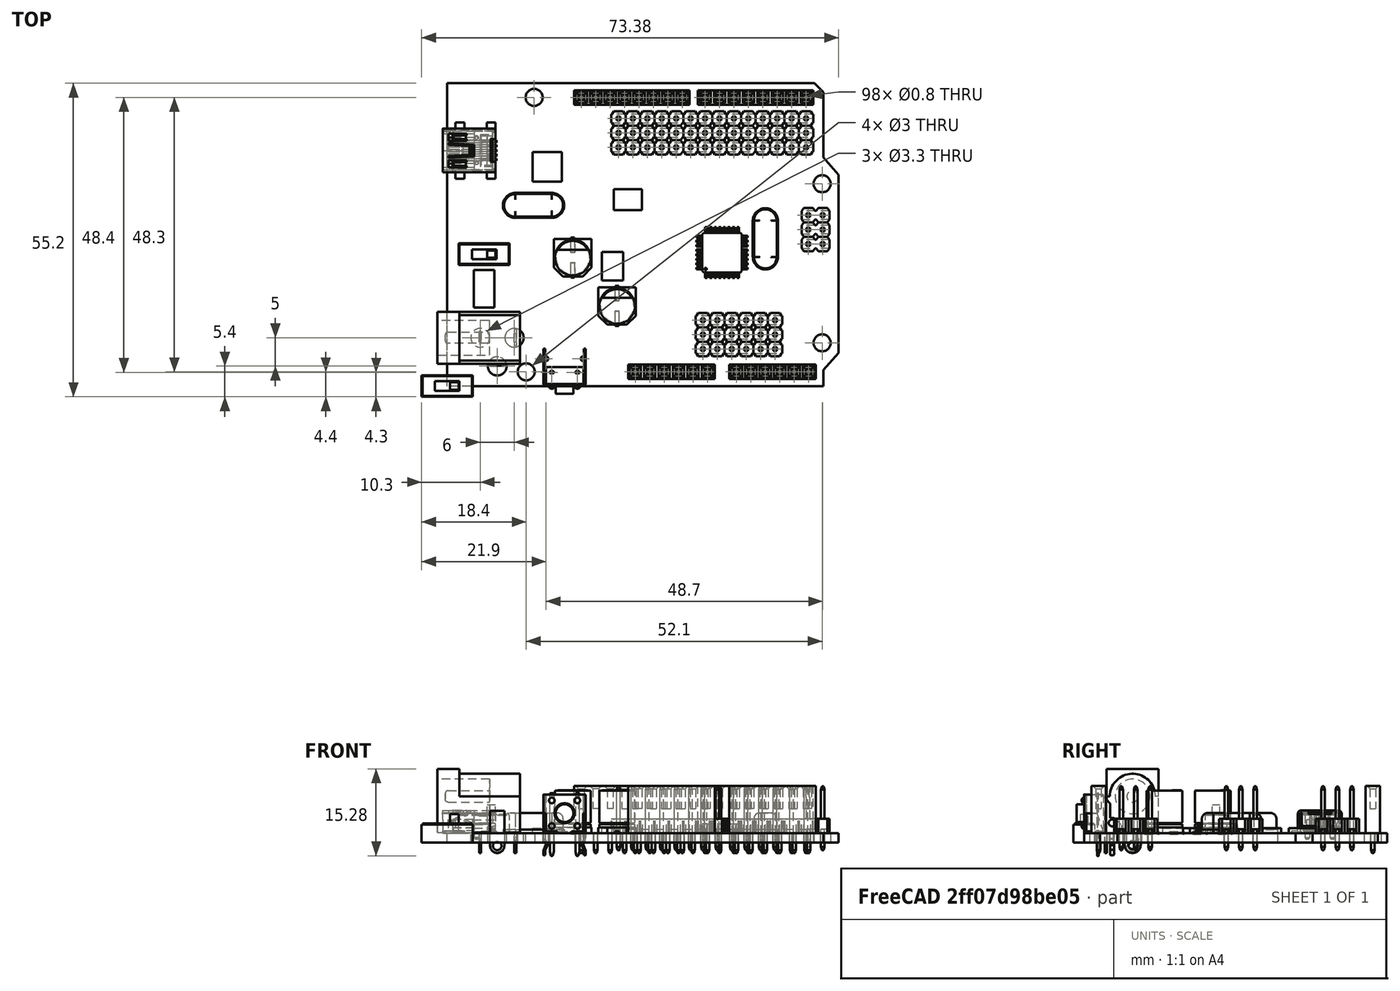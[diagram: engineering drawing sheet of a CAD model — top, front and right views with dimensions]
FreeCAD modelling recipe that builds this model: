
FCSTD DOCUMENT  (FreeCAD 0.14R3702 (Git))
Label: freaduino-uno
License: CC-BY 3.0
LicenseURL: http://creativecommons.org/licenses/by/3.0/
objects: Part::Compound×19, Part::FeaturePython×18, Part::Cylinder×12, Sketcher::SketchObject×9, PartDesign::Pad×7, Part::Feature×3, Part::MultiFuse×3, App::DocumentObjectGroup×3, PartDesign::Pocket×2, Part::Cut×1
note: 83 computed .brp shape members not serialized (recipe doc carries the construction recipe); baked Part::Feature solids carry a one-line shape summary decoded from their .brp

FEATURE [Sketcher::SketchObject] Sketch  label="pcb-main-body-sketch"
  sketch-geometry (9):
    g0: LineSegment StartX=66.2 StartY=0 StartZ=0 EndX=0 EndY=0 EndZ=0
    g1: LineSegment StartX=0 StartY=0 StartZ=0 EndX=0 EndY=53.3 EndZ=0
    g2: LineSegment StartX=66.2 StartY=51.7 StartZ=0 EndX=66.2 EndY=40.2 EndZ=0
    g3: LineSegment StartX=66.2 StartY=40.2 StartZ=0 EndX=68.88 EndY=37.2 EndZ=0
    g4: LineSegment StartX=68.88 StartY=37.2 StartZ=0 EndX=68.88 EndY=5.8 EndZ=0
    g5: LineSegment StartX=68.88 StartY=5.8 StartZ=0 EndX=66.2 EndY=2.8 EndZ=0
    g6: LineSegment StartX=66.2 StartY=2.8 StartZ=0 EndX=66.2 EndY=0 EndZ=0
    g7: LineSegment StartX=0 StartY=53.3 StartZ=0 EndX=64.6 EndY=53.3 EndZ=0
    g8: LineSegment StartX=64.6 StartY=53.3 StartZ=0 EndX=66.2 EndY=51.7 EndZ=0
  constraints (26):
    c: Coincident(g0,g1)
    c: Horizontal(g0)
    c: Vertical(g1)
    c: Coincident(g0,g-1)
    c: Coincident(g2,g3)
    c: Coincident(g3,g4)
    c: Coincident(g4,g5)
    c: Coincident(g5,g6)
    c: Coincident(g6,g0)
    c: DistanceY(g1) = 53.3
    c: Vertical(g6)
    c: Vertical(g2)
    c: Vertical(g4)
    c: PointOnObject(g0,g2)
    c: DistanceY(g2,g3) = -3
    c: DistanceY(g2,g5) = -37.4
    c: DistanceX(g2,g3) = 2.68
    c: Coincident(g7,g8)
    c: Horizontal(g7)
    c: Coincident(g7,g1)
    c: Coincident(g8,g2)
    c: DistanceX(g2,g1) = -66.2
    c: Angle(g7,g8) = 2.35619
    c: DistanceX(g7,g2) = 1.6
    c: DistanceY(g2) = -11.5
    c: DistanceY(g4,g5) = -3
FEATURE [PartDesign::Pad] Pad  label="pcb-main-body"
  Length = 1.7
  Length2 = 100
  Sketch = -> Sketch
  Type = 0
FEATURE [Sketcher::SketchObject] Sketch001  label="pcb-attachment-drills-sketch"
  ExternalGeometry = -> [Pad]
  Placement = pos=(0,0,1.7) rot=(0,0,1;0rad)
  Support = -> Pad [Face11]
  sketch-geometry (5):
    g0: Circle CenterX=15.3 CenterY=50.8 CenterZ=0 NormalX=0 NormalY=0 NormalZ=1 Radius=1.5
    g1: Circle CenterX=13.9 CenterY=2.5 CenterZ=0 NormalX=0 NormalY=0 NormalZ=1 Radius=1.5
    g2: Circle CenterX=66 CenterY=35.6 CenterZ=0 NormalX=0 NormalY=0 NormalZ=1 Radius=1.5
    g3: Circle CenterX=66 CenterY=7.6 CenterZ=0 NormalX=0 NormalY=0 NormalZ=1 Radius=1.5
    g4: LineSegment [constr] StartX=66 StartY=35.6 StartZ=0 EndX=66 EndY=7.6 EndZ=0
  constraints (14):
    c: Radius(g1) = 1.5
    c: Equal(g1,g0)
    c: Equal(g0,g2)
    c: Equal(g2,g3)
    c: DistanceX(g-1,g1) = 13.9
    c: DistanceY(g-1,g1) = 2.5
    c: DistanceY(g-1,g0) = 50.8
    c: Vertical(g4)
    c: Coincident(g4,g2)
    c: Coincident(g4,g3)
    c: DistanceX(g-1,g0) = 15.3
    c: DistanceY(g4) = -28
    c: DistanceY(g1,g3) = 5.1
    c: DistanceX(g1,g3) = 52.1
FEATURE [PartDesign::Pocket] Pocket  label="pcb-attachment-drills"
  Length = 5
  Sketch = -> Sketch001
  Type = 1
FEATURE [Part::Cylinder] Cylinder
  Angle = 360
  Height = 10
  Placement = pos=(0,0,-4) rot=(0,0,1;0rad)
  Radius = 0.4
FEATURE [Part::FeaturePython] Array  label="drills-1"  # Draft array (typed FeaturePython)
  Angle = 360
  ArrayType = 0
  Axis = (0,0,1)
  Base = -> Cylinder
  Center = (0,0,0)
  IntervalX = (2.54,0,0)
  IntervalY = (0,1,0)
  IntervalZ = (0,0,1)
  NumberPolar = 1
  NumberX = 6
  NumberY = 1
  NumberZ = 1
  Placement = pos=(33.1,2.5,0) rot=(0,0,1;0rad)
FEATURE [Part::Feature] Array001  label="drills-002"
  Placement = pos=(50.9,2.5,0) rot=(0,0,1;0rad)
  shape: bbox 13.5 x 0.8 x 10 mm, 18 faces, 6 solids (baked)
FEATURE [Part::Cylinder] Cylinder001
  Angle = 360
  Height = 10
  Placement = pos=(0,0,-3) rot=(0,0,1;0rad)
  Radius = 0.4
FEATURE [Part::FeaturePython] Array002  label="drills-003"  # Draft array (typed FeaturePython)
  Angle = 360
  ArrayType = 0
  Axis = (0,0,1)
  Base = -> Cylinder001
  Center = (0,0,0)
  IntervalX = (2.54,0,0)
  IntervalY = (0,1,0)
  IntervalZ = (0,0,1)
  NumberPolar = 1
  NumberX = 8
  NumberY = 1
  NumberZ = 1
  Placement = pos=(23.6,50.8,0) rot=(0,0,1;0rad)
FEATURE [Part::Feature] Array002001  label="drills-004"
  Placement = pos=(45.38,50.8,0) rot=(0,0,1;0rad)
  shape: bbox 18.58 x 0.8 x 10 mm, 24 faces, 8 solids (baked)
FEATURE [Part::Cylinder] Cylinder002  label="cylinder"
  Angle = 360
  Height = 10
  Placement = pos=(63.16,47.1,-3) rot=(0,0,1;0rad)
  Radius = 0.4
FEATURE [Part::FeaturePython] Array002002  # Draft array (typed FeaturePython)
  Angle = 360
  ArrayType = 0
  Axis = (0,0,1)
  Base = -> Cylinder002
  Center = (0,0,0)
  IntervalX = (-2.54,0,0)
  IntervalY = (0,1,0)
  IntervalZ = (0,0,1)
  NumberPolar = 1
  NumberX = 14
  NumberY = 0
  NumberZ = 1
FEATURE [Part::FeaturePython] Array002003  label="drills-digital"  # Draft array (typed FeaturePython)
  Angle = 360
  ArrayType = 0
  Axis = (0,0,1)
  Base = -> Array002002
  Center = (0,0,0)
  IntervalX = (1,0,0)
  IntervalY = (0,-2.54,0)
  IntervalZ = (0,0,1)
  NumberPolar = 1
  NumberX = 1
  NumberY = 3
  NumberZ = 1
FEATURE [Part::Cylinder] Cylinder003  label="Cylinder002"
  Angle = 360
  Height = 10
  Placement = pos=(45,6.5,-3) rot=(0,0,1;0rad)
  Radius = 0.4
FEATURE [Part::FeaturePython] Array002004  # Draft array (typed FeaturePython)
  Angle = 360
  ArrayType = 0
  Axis = (0,0,1)
  Base = -> Cylinder003
  Center = (0,0,0)
  IntervalX = (2.54,0,0)
  IntervalY = (0,1,0)
  IntervalZ = (0,0,1)
  NumberPolar = 1
  NumberX = 6
  NumberY = 1
  NumberZ = 1
FEATURE [Part::FeaturePython] Array002005  label="drills-analog"  # Draft array (typed FeaturePython)
  Angle = 360
  ArrayType = 0
  Axis = (0,0,1)
  Base = -> Array002004
  Center = (0,0,0)
  IntervalX = (1,0,0)
  IntervalY = (0,2.54,0)
  IntervalZ = (0,0,1)
  NumberPolar = 1
  NumberX = 1
  NumberY = 3
  NumberZ = 1
FEATURE [Part::Cylinder] Cylinder004  label="Cylinder003"
  Angle = 360
  Height = 10
  Placement = pos=(66.1,25,-3) rot=(0,0,1;0rad)
  Radius = 0.4
FEATURE [Part::FeaturePython] Array002006  # Draft array (typed FeaturePython)
  Angle = 360
  ArrayType = 0
  Axis = (0,0,1)
  Base = -> Cylinder004
  Center = (0,0,0)
  IntervalX = (-2.54,0,0)
  IntervalY = (0,0,0)
  IntervalZ = (0,0,1)
  NumberPolar = 1
  NumberX = 2
  NumberY = 1
  NumberZ = 1
FEATURE [Part::FeaturePython] Array002007  label="drills-icsp"  # Draft array (typed FeaturePython)
  Angle = 360
  ArrayType = 0
  Axis = (0,0,1)
  Base = -> Array002006
  Center = (0,0,0)
  IntervalX = (1,0,0)
  IntervalY = (0,2.54,0)
  IntervalZ = (0,0,1)
  NumberPolar = 1
  NumberX = 1
  NumberY = 3
  NumberZ = 1
FEATURE [Part::Cylinder] Cylinder005  label="Cylinder004"
  Angle = 360
  Height = 10
  Placement = pos=(18.4,2.4,-3) rot=(0,0,1;0rad)
  Radius = 0.4
FEATURE [Part::Cylinder] Cylinder006  label="Cylinder005"
  Angle = 360
  Height = 10
  Placement = pos=(22.91,2.4,-3) rot=(0,0,1;0rad)
  Radius = 0.4
FEATURE [Part::Cylinder] Cylinder007  label="Cylinder006"
  Angle = 360
  Height = 10
  Placement = pos=(17.4,4.8,-3) rot=(0,0,1;0rad)
  Radius = 0.4
FEATURE [Part::Cylinder] Cylinder008  label="Cylinder007"
  Angle = 360
  Height = 10
  Placement = pos=(23.91,4.8,-3) rot=(0,0,1;0rad)
  Radius = 0.4
FEATURE [Part::MultiFuse] Fusion  label="reset-button-drills"
  Shapes = -> [Cylinder005,Cylinder006,Cylinder007,Cylinder008]
FEATURE [Part::Cylinder] Cylinder009  label="Cylinder008"
  Angle = 360
  Height = 10
  Placement = pos=(0,0,-3) rot=(0,0,1;0rad)
  Radius = 1.65
FEATURE [Part::Cylinder] Cylinder010  label="Cylinder009"
  Angle = 360
  Height = 10
  Placement = pos=(3,5,-3) rot=(0,0,1;0rad)
  Radius = 1.65
FEATURE [Part::Cylinder] Cylinder011  label="Cylinder010"
  Angle = 360
  Height = 10
  Placement = pos=(-3,5,-3) rot=(0,0,1;0rad)
  Radius = 1.65
FEATURE [Part::MultiFuse] Fusion001  label="power-jack-drills"
  Placement = pos=(8.8,3.5,0) rot=(0,0,1;0rad)
  Shapes = -> [Cylinder009,Cylinder011,Cylinder010]
FEATURE [Part::MultiFuse] Fusion002  label="cylinders-drills"
  Shapes = -> [Array,Array002003,Array002,Array002001,Array001,Array002005,Array002007,Fusion001,Fusion]
FEATURE [Part::Cut] Cut  label="pcb-with-drills"
  Base = -> Pocket
  Tool = -> Fusion002
FEATURE [Part::Compound] Compound  label="1x6-female-pin-header"
  Placement = pos=(50.9,2.5,1.7) rot=(0,0,1;0rad)
FEATURE [Part::Compound] Compound001  label="1x6-female-pin-header001"
  Placement = pos=(33.1,2.5,1.7) rot=(0,0,1;0rad)
FEATURE [Part::Compound] Compound002  label="1x8-female-pin-header"
  Placement = pos=(45.4,50.8,1.7) rot=(0,0,1;0rad)
FEATURE [Part::Compound] Compound003  label="1x8-female-pin-header001"
  Placement = pos=(23.6,50.8,1.7) rot=(0,0,1;0rad)
FEATURE [Part::Compound] Compound004  label="1x14-male-pin-header"
  Placement = pos=(30.14,47.1,1.7) rot=(0,0,1;0rad)
FEATURE [Part::Compound] Compound005  label="1x14-male-pin-header001"
  Placement = pos=(30.14,42.02,1.7) rot=(0,0,1;0rad)
FEATURE [Part::Compound] Compound006  label="1x14-male-pin-header002"
  Placement = pos=(30.14,44.56,1.698) rot=(0,0,1;0rad)
FEATURE [Part::Compound] Compound007  label="1x6-male-pin-header"
  Links = -> [Array001,Array002001]
  Placement = pos=(45,6.5,1.7) rot=(0,0,1;0rad)
FEATURE [Part::Compound] Compound008  label="1x6-male-pin-header001"
  Links = -> [Array001,Array002001]
  Placement = pos=(45,9.04,1.7) rot=(0,0,1;0rad)
FEATURE [Part::Compound] Compound009  label="1x6-male-pin-header002"
  Links = -> [Array001,Array002001]
  Placement = pos=(45,11.58,1.7) rot=(0,0,1;0rad)
FEATURE [Part::Compound] Compound010  label="2x3-male-pin-header"
  Placement = pos=(64.83,27.54,1.7) rot=(0,0,1;0rad)
FEATURE [Part::Compound] Compound011  label="pushbutton-right-angle"
  Placement = pos=(20.6546,4.9,1.69239) rot=(0,0,1;0rad)
FEATURE [Part::Feature] Fusion003  label="jack_DC_2.1mm_PCB-final"
  Placement = pos=(-1.7,8.5,1.8) rot=(0.57735,-0.57735,-0.57735;2.0944rad)
  shape: bbox 14.48 x 9.472 x 14.78 mm, 34 faces (baked)
FEATURE [Part::Compound] Compound012  label="micro-usb-b-female-smd"
  Placement = pos=(8,41.45,1.7667) rot=(0.57735,-0.57735,-0.57735;2.0944rad)
FEATURE [Part::FeaturePython] Clone  label="Xtal"  # WARN: FeaturePython — macro-defined, semantics opaque (R4)
  Placement = pos=(15.2,31.8,1) rot=(0,0,1;0rad)
  Scale = (1,1,1)
FEATURE [Part::FeaturePython] Clone001  label="Xtal001"  # WARN: FeaturePython — macro-defined, semantics opaque (R4)
  Placement = pos=(56,25.9,1) rot=(0,0,1;1.5708rad)
  Scale = (1,1,1)
FEATURE [Part::Compound] Compound013  label="PQFP-32"
  Placement = pos=(43.86,19,1.7) rot=(0,0,1;0rad)
FEATURE [Sketcher::SketchObject] Sketch002  label="switch-body-sketch"
  sketch-geometry (4):
    g0: LineSegment StartX=-4.5 StartY=1.9 StartZ=0 EndX=4.5 EndY=1.9 EndZ=0
    g1: LineSegment StartX=4.5 StartY=1.9 StartZ=0 EndX=4.5 EndY=-1.9 EndZ=0
    g2: LineSegment StartX=4.5 StartY=-1.9 StartZ=0 EndX=-4.5 EndY=-1.9 EndZ=0
    g3: LineSegment StartX=-4.5 StartY=-1.9 StartZ=0 EndX=-4.5 EndY=1.9 EndZ=0
  constraints (11):
    c: Coincident(g0,g1)
    c: Coincident(g1,g2)
    c: Coincident(g2,g3)
    c: Coincident(g3,g0)
    c: Horizontal(g0)
    c: Horizontal(g2)
    c: Vertical(g1)
    c: Vertical(g3)
    c: DistanceX(g0) = 9
    c: DistanceY(g1) = -3.8
    c: Symmetric(g0,g1,g-1)
FEATURE [PartDesign::Pad] Pad001  label="switch-body"
  Length = 3.2
  Length2 = 100
  Sketch = -> Sketch002
  Type = 0
FEATURE [Sketcher::SketchObject] Sketch003  label="switch-top-plate-body-sketch"
  Placement = pos=(0,0,3.2) rot=(0,0,1;0rad)
  sketch-geometry (4):
    g0: LineSegment StartX=-4.35 StartY=1.725 StartZ=0 EndX=4.35 EndY=1.725 EndZ=0
    g1: LineSegment StartX=4.35 StartY=1.725 StartZ=0 EndX=4.35 EndY=-1.725 EndZ=0
    g2: LineSegment StartX=4.35 StartY=-1.725 StartZ=0 EndX=-4.35 EndY=-1.725 EndZ=0
    g3: LineSegment StartX=-4.35 StartY=-1.725 StartZ=0 EndX=-4.35 EndY=1.725 EndZ=0
  constraints (11):
    c: Coincident(g0,g1)
    c: Coincident(g1,g2)
    c: Coincident(g2,g3)
    c: Coincident(g3,g0)
    c: Horizontal(g0)
    c: Horizontal(g2)
    c: Vertical(g1)
    c: Vertical(g3)
    c: Symmetric(g0,g1,g-1)
    c: DistanceX(g0) = 8.7
    c: DistanceY(g1) = -3.45
FEATURE [PartDesign::Pad] Pad002  label="switch-top-plate-body"
  Length = 0.2
  Length2 = 100
  Placement = pos=(0,0,3.2) rot=(0,0,1;0rad)
  Sketch = -> Sketch003
  Type = 0
FEATURE [Sketcher::SketchObject] Sketch004  label="switch-top-plate-cutout-sketch"
  Placement = pos=(0,0,3.4) rot=(0,0,1;0rad)
  Support = -> Pad002 [Face6]
  sketch-geometry (4):
    g0: LineSegment StartX=-2.15 StartY=0.85 StartZ=0 EndX=2.15 EndY=0.85 EndZ=0
    g1: LineSegment StartX=2.15 StartY=0.85 StartZ=0 EndX=2.15 EndY=-0.85 EndZ=0
    g2: LineSegment StartX=2.15 StartY=-0.85 StartZ=0 EndX=-2.15 EndY=-0.85 EndZ=0
    g3: LineSegment StartX=-2.15 StartY=-0.85 StartZ=0 EndX=-2.15 EndY=0.85 EndZ=0
  constraints (11):
    c: Coincident(g0,g1)
    c: Coincident(g1,g2)
    c: Coincident(g2,g3)
    c: Coincident(g3,g0)
    c: Horizontal(g0)
    c: Horizontal(g2)
    c: Vertical(g1)
    c: Vertical(g3)
    c: Symmetric(g0,g1,g-1)
    c: DistanceX(g0) = 4.3
    c: DistanceY(g1) = -1.7
FEATURE [PartDesign::Pocket] Pocket001  label="switch-top-plate-cutout"
  Length = 5
  Placement = pos=(0,0,3.2) rot=(0,0,1;0rad)
  Sketch = -> Sketch004
  Type = 1
FEATURE [Sketcher::SketchObject] Sketch005  label="switch-sketch"
  Placement = pos=(0,0,3.2) rot=(0,0,1;0rad)
  Support = -> Pad001 [Face6]
  sketch-geometry (4):
    g0: LineSegment StartX=0.5 StartY=0.65 StartZ=0 EndX=2 EndY=0.65 EndZ=0
    g1: LineSegment StartX=2 StartY=0.65 StartZ=0 EndX=2 EndY=-0.65 EndZ=0
    g2: LineSegment StartX=2 StartY=-0.65 StartZ=0 EndX=0.5 EndY=-0.65 EndZ=0
    g3: LineSegment StartX=0.5 StartY=-0.65 StartZ=0 EndX=0.5 EndY=0.65 EndZ=0
  constraints (12):
    c: Coincident(g0,g1)
    c: Coincident(g1,g2)
    c: Coincident(g2,g3)
    c: Coincident(g3,g0)
    c: Horizontal(g0)
    c: Horizontal(g2)
    c: Vertical(g1)
    c: Vertical(g3)
    c: Symmetric(g2,g0,g-1)
    c: DistanceX(g0) = 1.5
    c: DistanceY(g1) = -1.3
    c: DistanceX(g-1,g2) = 0.5
FEATURE [PartDesign::Pad] Pad003  label="switch"
  Length = 1.86
  Length2 = 100
  Sketch = -> Sketch005
  Type = 0
FEATURE [Part::FeaturePython] Clone002  label="switch-top-plate"  # Draft clone (typed FeaturePython)
  Objects = -> [Pocket001]
  Placement = pos=(0,0,3.2) rot=(0,0,1;0rad)
  Scale = (1,1,1)
FEATURE [Part::FeaturePython] Clone003  label="switch-body001"  # Draft clone (typed FeaturePython)
  Objects = -> [Pad003]
  Scale = (1,1,1)
FEATURE [Part::Compound] Compound014  label="switch-final-1"
  Links = -> [Clone002,Clone003]
FEATURE [App::DocumentObjectGroup] Group  label="switch-src"
  Group = -> [Pad001,Pad002,Pocket001,Pad003,Compound014]
FEATURE [Part::Compound] Compound015  label="switch-final-002"
  Placement = pos=(6.5,23.2,1.65) rot=(0,0,1;0rad)
FEATURE [Part::Compound] Compound016  label="capsmd-6x7"
  Placement = pos=(29.9,14.1,2.7) rot=(0,0,1;3.14159rad)
FEATURE [Part::Compound] Compound017  label="capsmd-6x008"
  Placement = pos=(22.1,22.6,2.7) rot=(0,0,1;3.14159rad)
FEATURE [Sketcher::SketchObject] Sketch006  label="chip-1-sketch"
  sketch-geometry (4):
    g0: LineSegment StartX=-2.6 StartY=2.6 StartZ=0 EndX=2.6 EndY=2.6 EndZ=0
    g1: LineSegment StartX=2.6 StartY=2.6 StartZ=0 EndX=2.6 EndY=-2.6 EndZ=0
    g2: LineSegment StartX=2.6 StartY=-2.6 StartZ=0 EndX=-2.6 EndY=-2.6 EndZ=0
    g3: LineSegment StartX=-2.6 StartY=-2.6 StartZ=0 EndX=-2.6 EndY=2.6 EndZ=0
  constraints (11):
    c: Coincident(g0,g1)
    c: Coincident(g1,g2)
    c: Coincident(g2,g3)
    c: Coincident(g3,g0)
    c: Horizontal(g0)
    c: Horizontal(g2)
    c: Vertical(g1)
    c: Vertical(g3)
    c: Symmetric(g0,g1,g-1)
    c: DistanceX(g0) = 5.2
    c: Equal(g0,g1)
FEATURE [PartDesign::Pad] Pad004  label="chip-src-1"
  Length = 0.9
  Length2 = 100
  Sketch = -> Sketch006
  Type = 0
FEATURE [Part::FeaturePython] Clone004  label="chip-1"  # Draft clone (typed FeaturePython)
  Objects = -> [Pad004]
  Placement = pos=(17.6,38.6,1.65) rot=(0,0,1;0rad)
  Scale = (1,1,1)
FEATURE [Sketcher::SketchObject] Sketch007  label="chip-src-2-sketch"
  sketch-geometry (4):
    g0: LineSegment StartX=-1.8 StartY=3.3 StartZ=0 EndX=1.8 EndY=3.3 EndZ=0
    g1: LineSegment StartX=1.8 StartY=3.3 StartZ=0 EndX=1.8 EndY=-3.3 EndZ=0
    g2: LineSegment StartX=1.8 StartY=-3.3 StartZ=0 EndX=-1.8 EndY=-3.3 EndZ=0
    g3: LineSegment StartX=-1.8 StartY=-3.3 StartZ=0 EndX=-1.8 EndY=3.3 EndZ=0
  constraints (11):
    c: Coincident(g0,g1)
    c: Coincident(g1,g2)
    c: Coincident(g2,g3)
    c: Coincident(g3,g0)
    c: Horizontal(g0)
    c: Horizontal(g2)
    c: Vertical(g1)
    c: Vertical(g3)
    c: Symmetric(g1,g0,g-1)
    c: DistanceX(g0) = 3.6
    c: DistanceY(g1) = -6.6
FEATURE [PartDesign::Pad] Pad005  label="chip-src-2"
  Length = 0.9
  Length2 = 100
  Sketch = -> Sketch007
  Type = 0
FEATURE [Part::FeaturePython] Clone005  label="chip-2"  # Draft clone (typed FeaturePython)
  Objects = -> [Pad005]
  Placement = pos=(6.5,17.1,1.65) rot=(0,0,1;0rad)
  Scale = (1,1,1)
FEATURE [Sketcher::SketchObject] Sketch008  label="chip-src-3-sketch"
  sketch-geometry (4):
    g0: LineSegment StartX=-2.5 StartY=1.85 StartZ=0 EndX=2.5 EndY=1.85 EndZ=0
    g1: LineSegment StartX=2.5 StartY=1.85 StartZ=0 EndX=2.5 EndY=-1.85 EndZ=0
    g2: LineSegment StartX=2.5 StartY=-1.85 StartZ=0 EndX=-2.5 EndY=-1.85 EndZ=0
    g3: LineSegment StartX=-2.5 StartY=-1.85 StartZ=0 EndX=-2.5 EndY=1.85 EndZ=0
  constraints (11):
    c: Coincident(g0,g1)
    c: Coincident(g1,g2)
    c: Coincident(g2,g3)
    c: Coincident(g3,g0)
    c: Horizontal(g0)
    c: Horizontal(g2)
    c: Vertical(g1)
    c: Vertical(g3)
    c: Symmetric(g0,g1,g-1)
    c: DistanceX(g0) = 5
    c: DistanceY(g1) = -3.7
FEATURE [PartDesign::Pad] Pad006  label="chip-src-3"
  Length = 0.9
  Length2 = 100
  Sketch = -> Sketch008
  Type = 0
FEATURE [App::DocumentObjectGroup] Group001  label="more-chips"
  Group = -> [Pad004,Pad005,Pad006]
FEATURE [Part::FeaturePython] Clone006  label="chip-3"  # Draft clone (typed FeaturePython)
  Objects = -> [Pad006]
  Placement = pos=(31.8,32.8,1.65) rot=(0,0,1;0rad)
  Scale = (1,1,1)
FEATURE [Part::FeaturePython] Clone007  label="chip-4"  # Draft clone (typed FeaturePython)
  Objects = -> [Clone006]
  Placement = pos=(29.1,21.1,1.65) rot=(0,0,1;1.5708rad)
  Scale = (1,1,1)
FEATURE [App::DocumentObjectGroup] Group002  label="pcb-src"
  Group = -> [Pad,Cut,Compound009]
FEATURE [Part::FeaturePython] Clone008  label="pcb-with-drills001"  # Draft clone (typed FeaturePython)
  Objects = -> [Cut]
  Scale = (1,1,1)
FEATURE [Part::FeaturePython] Clone009  label="1x6-male-pin-header003"  # Draft clone (typed FeaturePython)
  Objects = -> [Compound009]
  Placement = pos=(45,11.58,1.7) rot=(0,0,1;0rad)
  Scale = (1,1,1)
FEATURE [Part::Compound] Compound018  label="freaduino-uno"
  Links = -> [Clone008,Compound,Compound001,Compound002,Compound003,Compound004,Compound005,Compound006,Compound007,Compound008,Compound010,Compound011,Fusion003,Compound012,Clone,Clone001,Compound013,Clone004,Compound015,Compound017,Clone009,Clone007,Clone005,Compound016,Clone006]
